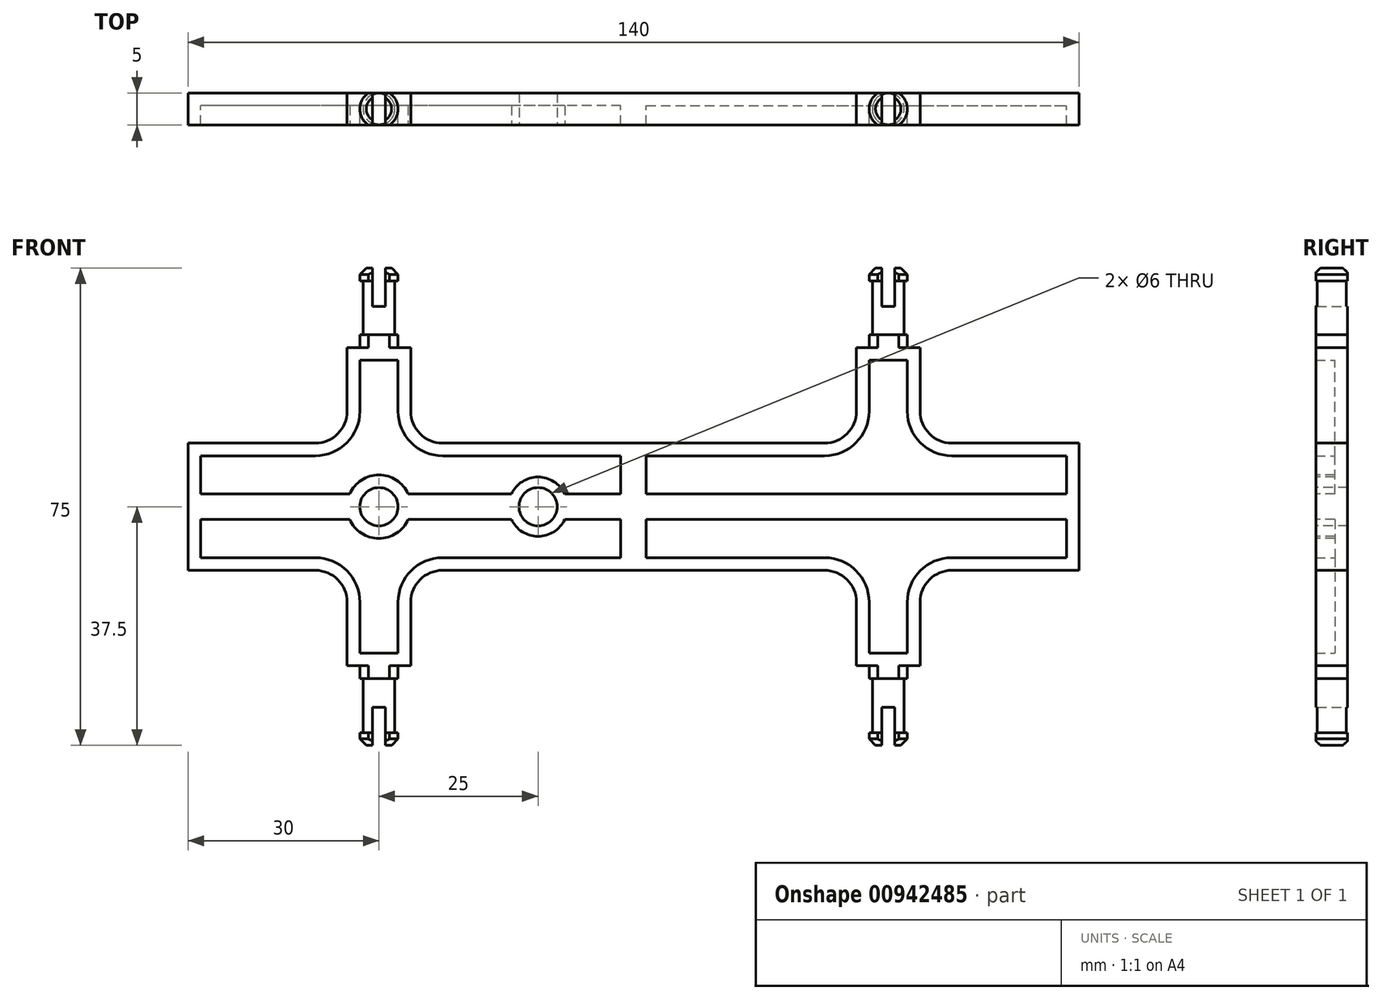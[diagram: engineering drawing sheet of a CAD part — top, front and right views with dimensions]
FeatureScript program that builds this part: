
annotation { "Feature Type Name" : "Feature", "Feature Type Description" : "" }
export const myFeature = defineFeature(function(context is Context, id is Id, definition is map)
    precondition{}
    {
        {
            var Q0;
            Q0=qCreatedBy(makeId("Front.planeOp"),FACE);
            var sketch = newSketch(context, id + "F0", { "sketchPlane" : qUnion([Q0])});
            skLineSegment(sketch, "E0.bottom", {"start": v(0, 0) * mm, "end": v(70, 0) * mm});
            skLineSegment(sketch, "E0.top", {"start": v(0, 10) * mm, "end": v(30, 10) * mm});
            skLineSegment(sketch, "E0.left", {"start": v(0, 0) * mm, "end": v(0, 10) * mm});
            skLineSegment(sketch, "E0.right", {"start": v(70, 0) * mm, "end": v(70, 10) * mm});
            skLineSegment(sketch, "E1.top", {"start": v(35, 25) * mm, "end": v(45, 25) * mm});
            skLineSegment(sketch, "E1.left", {"start": v(35, 15) * mm, "end": v(35, 25) * mm});
            skLineSegment(sketch, "E1.right", {"start": v(45, 15) * mm, "end": v(45, 25) * mm});
            skLineSegment(sketch, "E2.trimOffspring", {"start": v(50, 10) * mm, "end": v(70, 10) * mm});
            skPoint(sketch, "E3.visualSharp", {"position": v(35, 10) * mm});
            skArc(sketch, "E3.filletArc", {"start": v(30, 10) * mm, "mid": v(33.54, 11.46) * mm, "end": v(35, 15) * mm});
            skPoint(sketch, "E4.visualSharp", {"position": v(45, 10) * mm});
            skArc(sketch, "E4.filletArc", {"start": v(45, 15) * mm, "mid": v(46.46, 11.46) * mm, "end": v(50, 10) * mm});
            skSolve(sketch);
        }
        {
            var Q0;
            Q0 = qSketchRegion(id + "F0", true);
            extrude(context, id + "F1", {"entities" : qUnion([Q0]), "endBound" : BoundingType.SYMMETRIC, "depth" : 5 * mm, "offsetDistance" : 25 * mm});
        }
        {
            var Q0;
            Q0=makeQuery(id+"F1.opExtrude","CAP_FACE",FACE,{"disambiguationData":[OSD([sQuery(id+"F0.wireOp",EDGE,"E0.bottom"),sQuery(id+"F0.wireOp",EDGE,"E0.top"),sQuery(id+"F0.wireOp",EDGE,"E0.left"),sQuery(id+"F0.wireOp",EDGE,"E0.right"),sQuery(id+"F0.wireOp",EDGE,"E1.top"),sQuery(id+"F0.wireOp",EDGE,"E1.left"),sQuery(id+"F0.wireOp",EDGE,"E1.right"),sQuery(id+"F0.wireOp",EDGE,"E2.trimOffspring"),sQuery(id+"F0.wireOp",EDGE,"E3.filletArc"),sQuery(id+"F0.wireOp",EDGE,"E4.filletArc")])],"isStart":false});
            shell(context, id + "F2", {"entities" : qUnion([Q0]), "thickness" : 2 * mm});
        }
        {
            var Q0;
            Q0=qCreatedBy(makeId("Front.planeOp"),FACE);
            var sketch = newSketch(context, id + "F3", { "sketchPlane" : qUnion([Q0])});
            skLineSegment(sketch, "E5", {"start": v(37, 37.5) * mm, "end": v(40, 37.5) * mm});
            skLineSegment(sketch, "E6", {"start": v(40, 37.5) * mm, "end": v(40, 25) * mm});
            skLineSegment(sketch, "E7", {"start": v(40, 25) * mm, "end": v(37, 25) * mm});
            skLineSegment(sketch, "E8", {"start": v(37, 25) * mm, "end": v(37, 27) * mm});
            skLineSegment(sketch, "E9", {"start": v(37, 27) * mm, "end": v(37.5, 27) * mm});
            skLineSegment(sketch, "E10", {"start": v(37.5, 27) * mm, "end": v(37.5, 35.5) * mm});
            skLineSegment(sketch, "E11", {"start": v(37.5, 35.5) * mm, "end": v(37, 35.5) * mm});
            skLineSegment(sketch, "E12", {"start": v(37, 35.5) * mm, "end": v(37, 37.5) * mm});
            skSolve(sketch);
        }
        {
            var Q0;
            Q0 = qSketchRegion(id + "F3", true);
            var Q1;
            Q1=sQuery(id+"F3.wireOp",EDGE,"E6");
            revolve(context, id + "F4", {"operationType" : NewBodyOperationType.ADD, "surfaceOperationType" : NewSurfaceOperationType.NEW, "entities" : qUnion([Q0]), "axis" : qUnion([Q1]), "revolveType" : RevolveType.FULL});
        }
        {
            var Q0;
            Q0=makeQuery(id+"F4.opRevolve","SWEPT_EDGE",EDGE,{"disambiguationData":[OSD([sQuery(id+"F3.wireOp",EDGE,"E5"),sQuery(id+"F3.wireOp",EDGE,"E12")])]});
            chamfer(context, id + "F5", {"entities" : qUnion([Q0]), "width" : 1 * mm, "tangentPropagation" : true});
        }
        {
            var Q0;
            Q0=makeQuery(id+"F4.opRevolve","SWEPT_FACE",FACE,{"disambiguationData":[OSD([sQuery(id+"F3.wireOp",EDGE,"E5")])]});
            var sketch = newSketch(context, id + "F6", { "sketchPlane" : qUnion([Q0])});
            skLineSegment(sketch, "E13.bottom", {"start": v(-2.96, -2.5) * mm, "end": v(72.2, -2.5) * mm});
            skLineSegment(sketch, "E13.top", {"start": v(-2.96, 2.5) * mm, "end": v(72.2, 2.5) * mm});
            skLineSegment(sketch, "E13.left", {"start": v(-2.96, -2.5) * mm, "end": v(-2.96, 2.5) * mm});
            skLineSegment(sketch, "E13.right", {"start": v(72.2, -2.5) * mm, "end": v(72.2, 2.5) * mm});
            skSolve(sketch);
        }
        {
            var Q0;
            Q0 = qSketchRegion(id + "F6", true);
            extrude(context, id + "F7", {"entities" : qUnion([Q0]), "operationType" : NewBodyOperationType.INTERSECT, "endBound" : BoundingType.THROUGH_ALL, "oppositeDirection" : true, "depth" : 25 * mm, "offsetDistance" : 25 * mm});
        }
        {
            var Q0;
            Q0=makeQuery(id+"F4.opRevolve","SWEPT_FACE",FACE,{"disambiguationData":[OSD([sQuery(id+"F3.wireOp",EDGE,"E5")])]});
            var sketch = newSketch(context, id + "F8", { "sketchPlane" : qUnion([Q0])});
            skLineSegment(sketch, "E14.bottom", {"start": v(39, -4.9) * mm, "end": v(41, -4.9) * mm});
            skLineSegment(sketch, "E14.top", {"start": v(39, 5.1) * mm, "end": v(41, 5.1) * mm});
            skLineSegment(sketch, "E14.left", {"start": v(39, -4.9) * mm, "end": v(39, 5.1) * mm});
            skLineSegment(sketch, "E14.right", {"start": v(41, -4.9) * mm, "end": v(41, 5.1) * mm});
            skSolve(sketch);
        }
        {
            var Q0;
            Q0 = qSketchRegion(id + "F8", true);
            extrude(context, id + "F9", {"entities" : qUnion([Q0]), "operationType" : NewBodyOperationType.REMOVE, "oppositeDirection" : true, "depth" : 6 * mm, "offsetDistance" : 25 * mm});
        }
        {
            var Q0;
            Q0=makeQuery(id+"F1.opExtrude","SWEPT_BODY",BODY,{"disambiguationData":[OSD([sQuery(id+"F0.wireOp",EDGE,"E0.bottom"),sQuery(id+"F0.wireOp",EDGE,"E0.top"),sQuery(id+"F0.wireOp",EDGE,"E0.left"),sQuery(id+"F0.wireOp",EDGE,"E0.right"),sQuery(id+"F0.wireOp",EDGE,"E1.top"),sQuery(id+"F0.wireOp",EDGE,"E1.left"),sQuery(id+"F0.wireOp",EDGE,"E1.right"),sQuery(id+"F0.wireOp",EDGE,"E2.trimOffspring"),sQuery(id+"F0.wireOp",EDGE,"E3.filletArc"),sQuery(id+"F0.wireOp",EDGE,"E4.filletArc")])]});
            var Q1;
            Q1=qCreatedBy(makeId("Top.planeOp"),FACE);
            mirror(context, id + "F10", {"operationType" : NewBodyOperationType.ADD, "entities" : qUnion([Q0]), "mirrorPlane" : qUnion([Q1])});
        }
        {
            var Q0;
            Q0=makeQuery(id+"F1.opExtrude","SWEPT_BODY",BODY,{"disambiguationData":[OSD([sQuery(id+"F0.wireOp",EDGE,"E0.bottom"),sQuery(id+"F0.wireOp",EDGE,"E0.top"),sQuery(id+"F0.wireOp",EDGE,"E0.left"),sQuery(id+"F0.wireOp",EDGE,"E0.right"),sQuery(id+"F0.wireOp",EDGE,"E1.top"),sQuery(id+"F0.wireOp",EDGE,"E1.left"),sQuery(id+"F0.wireOp",EDGE,"E1.right"),sQuery(id+"F0.wireOp",EDGE,"E2.trimOffspring"),sQuery(id+"F0.wireOp",EDGE,"E3.filletArc"),sQuery(id+"F0.wireOp",EDGE,"E4.filletArc")])]});
            var Q1;
            Q1=qCreatedBy(makeId("Right.planeOp"),FACE);
            mirror(context, id + "F11", {"operationType" : NewBodyOperationType.ADD, "entities" : qUnion([Q0]), "mirrorPlane" : qUnion([Q1])});
        }
        {
            var Q0;
            {var subQ0=makeQuery(id+"F7.boolean.opBoolean","MERGE",FACE,{"derivedFrom":[makeQuery(id+"F1.opExtrude","CAP_FACE",FACE,{"disambiguationData":[OSD([sQuery(id+"F0.wireOp",EDGE,"E0.bottom"),sQuery(id+"F0.wireOp",EDGE,"E0.top"),sQuery(id+"F0.wireOp",EDGE,"E0.left"),sQuery(id+"F0.wireOp",EDGE,"E0.right"),sQuery(id+"F0.wireOp",EDGE,"E1.top"),sQuery(id+"F0.wireOp",EDGE,"E1.left"),sQuery(id+"F0.wireOp",EDGE,"E1.right"),sQuery(id+"F0.wireOp",EDGE,"E2.trimOffspring"),sQuery(id+"F0.wireOp",EDGE,"E3.filletArc"),sQuery(id+"F0.wireOp",EDGE,"E4.filletArc")])],"isStart":false})],"fromTools":[makeQuery(id+"F7.boolean.toolComplement.opBoolean","COPY",FACE,{"derivedFrom":makeQuery(id+"F7.opExtrude","SWEPT_FACE",FACE,{"disambiguationData":[OSD([sQuery(id+"F6.wireOp",EDGE,"E13.bottom")])]})})]});var subQ1=makeQuery(id+"F10.boolean.opBoolean","MERGE",FACE,{"derivedFrom":[subQ0,makeQuery(id+"F10.opPattern","COPY",FACE,{"derivedFrom":subQ0,"instanceName":"1"})]});Q0=makeQuery(id+"F11.boolean.opBoolean","MERGE",FACE,{"derivedFrom":[subQ1,makeQuery(id+"F11.opPattern","COPY",FACE,{"derivedFrom":subQ1,"instanceName":"1"})]});}
            var sketch = newSketch(context, id + "F12", { "sketchPlane" : qUnion([Q0])});
            skCircle(sketch, "E15", {"center": v(-40, 0) * mm, "radius": 5 * mm});
            skCircle(sketch, "E16", {"center": v(-15, 0) * mm, "radius": 4.65 * mm});
            skSolve(sketch);
        }
        {
            var Q0;
            Q0 = qSketchRegion(id + "F12", true);
            extrude(context, id + "F13", {"entities" : qUnion([Q0]), "operationType" : NewBodyOperationType.ADD, "endBound" : BoundingType.UP_TO_NEXT, "oppositeDirection" : true, "depth" : 25 * mm, "offsetDistance" : 25 * mm});
        }
        {
            var Q0;
            {var subQ0=makeQuery(id+"F7.boolean.opBoolean","MERGE",FACE,{"derivedFrom":[makeQuery(id+"F1.opExtrude","CAP_FACE",FACE,{"disambiguationData":[OSD([sQuery(id+"F0.wireOp",EDGE,"E0.bottom"),sQuery(id+"F0.wireOp",EDGE,"E0.top"),sQuery(id+"F0.wireOp",EDGE,"E0.left"),sQuery(id+"F0.wireOp",EDGE,"E0.right"),sQuery(id+"F0.wireOp",EDGE,"E1.top"),sQuery(id+"F0.wireOp",EDGE,"E1.left"),sQuery(id+"F0.wireOp",EDGE,"E1.right"),sQuery(id+"F0.wireOp",EDGE,"E2.trimOffspring"),sQuery(id+"F0.wireOp",EDGE,"E3.filletArc"),sQuery(id+"F0.wireOp",EDGE,"E4.filletArc")])],"isStart":false})],"fromTools":[makeQuery(id+"F7.boolean.toolComplement.opBoolean","COPY",FACE,{"derivedFrom":makeQuery(id+"F7.opExtrude","SWEPT_FACE",FACE,{"disambiguationData":[OSD([sQuery(id+"F6.wireOp",EDGE,"E13.bottom")])]})})]});var subQ1=makeQuery(id+"F10.boolean.opBoolean","MERGE",FACE,{"derivedFrom":[subQ0,makeQuery(id+"F10.opPattern","COPY",FACE,{"derivedFrom":subQ0,"instanceName":"1"})]});Q0=makeQuery(id+"F13.boolean.opBoolean","MERGE",FACE,{"derivedFrom":[makeQuery(id+"F11.boolean.opBoolean","MERGE",FACE,{"derivedFrom":[subQ1,makeQuery(id+"F11.opPattern","COPY",FACE,{"derivedFrom":subQ1,"instanceName":"1"})]}),makeQuery(id+"F13.opExtrude","CAP_FACE",FACE,{"disambiguationData":[OSD([sQuery(id+"F12.wireOp",EDGE,"E15")])],"isStart":true}),makeQuery(id+"F13.opExtrude","CAP_FACE",FACE,{"disambiguationData":[OSD([sQuery(id+"F12.wireOp",EDGE,"E16")])],"isStart":true})]});}
            var sketch = newSketch(context, id + "F14", { "sketchPlane" : qUnion([Q0])});
            skPoint(sketch, "E17", {"position": v(-40, 0) * mm});
            skPoint(sketch, "E18", {"position": v(-15, 0) * mm});
            skSolve(sketch);
        }
        {
            var Q0;
            Q0=sQuery(id+"F14.wireOp",VERTEX,"E17");
            var Q1;
            Q1=sQuery(id+"F14.wireOp",VERTEX,"E18");
            var Q2;
            Q2=makeQuery(id+"F1.opExtrude","SWEPT_BODY",BODY,{"disambiguationData":[OSD([sQuery(id+"F0.wireOp",EDGE,"E0.bottom"),sQuery(id+"F0.wireOp",EDGE,"E0.top"),sQuery(id+"F0.wireOp",EDGE,"E0.left"),sQuery(id+"F0.wireOp",EDGE,"E0.right"),sQuery(id+"F0.wireOp",EDGE,"E1.top"),sQuery(id+"F0.wireOp",EDGE,"E1.left"),sQuery(id+"F0.wireOp",EDGE,"E1.right"),sQuery(id+"F0.wireOp",EDGE,"E2.trimOffspring"),sQuery(id+"F0.wireOp",EDGE,"E3.filletArc"),sQuery(id+"F0.wireOp",EDGE,"E4.filletArc")])]});
            hole(context, id + "F15", {"style" : HoleStyle.SIMPLE, "endStyle" : HoleEndStyle.THROUGH, "holeDiameter" : 6 * mm, "majorDiameter" : 5 * mm, "isTappedThrough" : true, "tappedDepth" : 12 * mm, "tapClearance" : 3, "locations" : qUnion([Q0, Q1]), "scope" : qUnion([Q2])});
        }
    });
